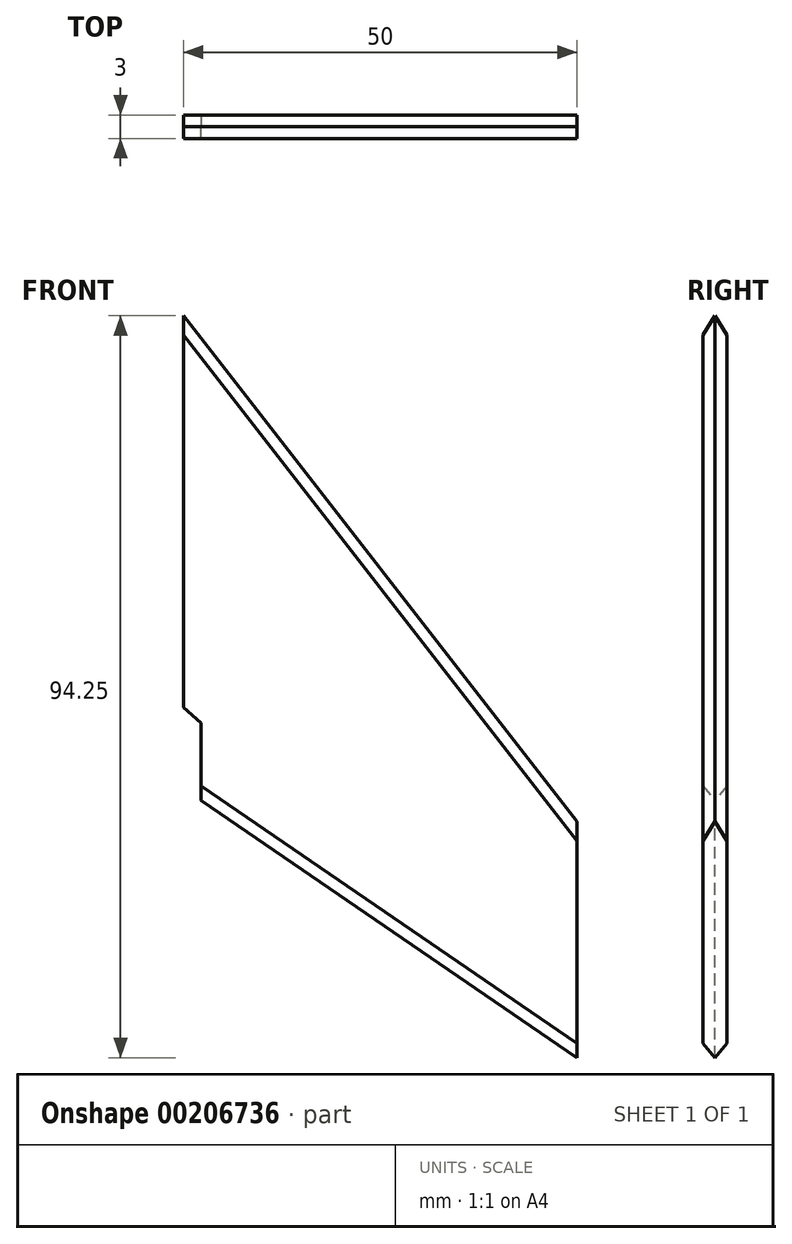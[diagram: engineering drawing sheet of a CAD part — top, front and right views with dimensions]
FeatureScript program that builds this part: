
annotation { "Feature Type Name" : "Feature", "Feature Type Description" : "" }
export const myFeature = defineFeature(function(context is Context, id is Id, definition is map)
    precondition{}
    {
        {
            var Q0;
            Q0=qCreatedBy(makeId("Front.planeOp"),FACE);
            var sketch = newSketch(context, id + "F0", { "sketchPlane" : qUnion([Q0])});
            skLineSegment(sketch, "E0", {"start": v(0, 0) * mm, "end": v(50, -34.25) * mm});
            skLineSegment(sketch, "E1", {"start": v(50, -34.25) * mm, "end": v(50, -4.25) * mm});
            skLineSegment(sketch, "E2", {"start": v(50, -4.25) * mm, "end": v(0, 60) * mm});
            skLineSegment(sketch, "E3", {"start": v(0, 60) * mm, "end": v(0, 0) * mm});
            skSolve(sketch);
        }
        {
            var Q0;
            Q0=makeQuery(id+"F0.imprint","IMPRINT",FACE,{"disambiguationData":[TD([[makeQuery(id+"F0.imprint","IMPRINT",EDGE,{"derivedFrom":sQuery(id+"F0.wireOp",EDGE,"E0")}),1.0]])]});
            extrude(context, id + "F1", {"entities" : qUnion([Q0]), "depth" : 3 * mm});
        }
        {
            var Q0;
            Q0=makeQuery(id+"F1.opExtrude","CAP_EDGE",EDGE,{"disambiguationData":[OSD([sQuery(id+"F0.wireOp",EDGE,"E2")])],"isStart":false});
            var Q1;
            Q1=makeQuery(id+"F1.opExtrude","CAP_EDGE",EDGE,{"disambiguationData":[OSD([sQuery(id+"F0.wireOp",EDGE,"E2")])],"isStart":true});
            var Q2;
            Q2=makeQuery(id+"F1.opExtrude","CAP_EDGE",EDGE,{"disambiguationData":[OSD([sQuery(id+"F0.wireOp",EDGE,"E0")])],"isStart":false});
            var Q3;
            Q3=makeQuery(id+"F1.opExtrude","CAP_EDGE",EDGE,{"disambiguationData":[OSD([sQuery(id+"F0.wireOp",EDGE,"E0")])],"isStart":true});
            chamfer(context, id + "F2", {"entities" : qUnion([Q0, Q1, Q2, Q3]), "width" : 1.5 * mm, "tangentPropagation" : true});
        }
        {
            var Q0;
            Q0=qCreatedBy(makeId("Front.planeOp"),FACE);
            var sketch = newSketch(context, id + "F3", { "sketchPlane" : qUnion([Q0])});
            skLineSegment(sketch, "E4", {"start": v(0, 10.25) * mm, "end": v(2.25, 8.25) * mm});
            skLineSegment(sketch, "E5", {"start": v(2.25, 8.25) * mm, "end": v(2.25, -5) * mm});
            skLineSegment(sketch, "E6", {"start": v(2.25, -5) * mm, "end": v(0, -5) * mm});
            skLineSegment(sketch, "E7", {"start": v(0, -5) * mm, "end": v(0, 10.25) * mm});
            skSolve(sketch);
        }
        {
            var Q0;
            Q0=makeQuery(id+"F3.imprint","IMPRINT",FACE,{"disambiguationData":[TD([[makeQuery(id+"F3.imprint","IMPRINT",EDGE,{"derivedFrom":sQuery(id+"F3.wireOp",EDGE,"E4")}),-1.0]])]});
            extrude(context, id + "F4", {"entities" : qUnion([Q0]), "operationType" : NewBodyOperationType.REMOVE, "endBound" : BoundingType.SYMMETRIC, "oppositeDirection" : true, "depth" : 8 * mm});
        }
    });
